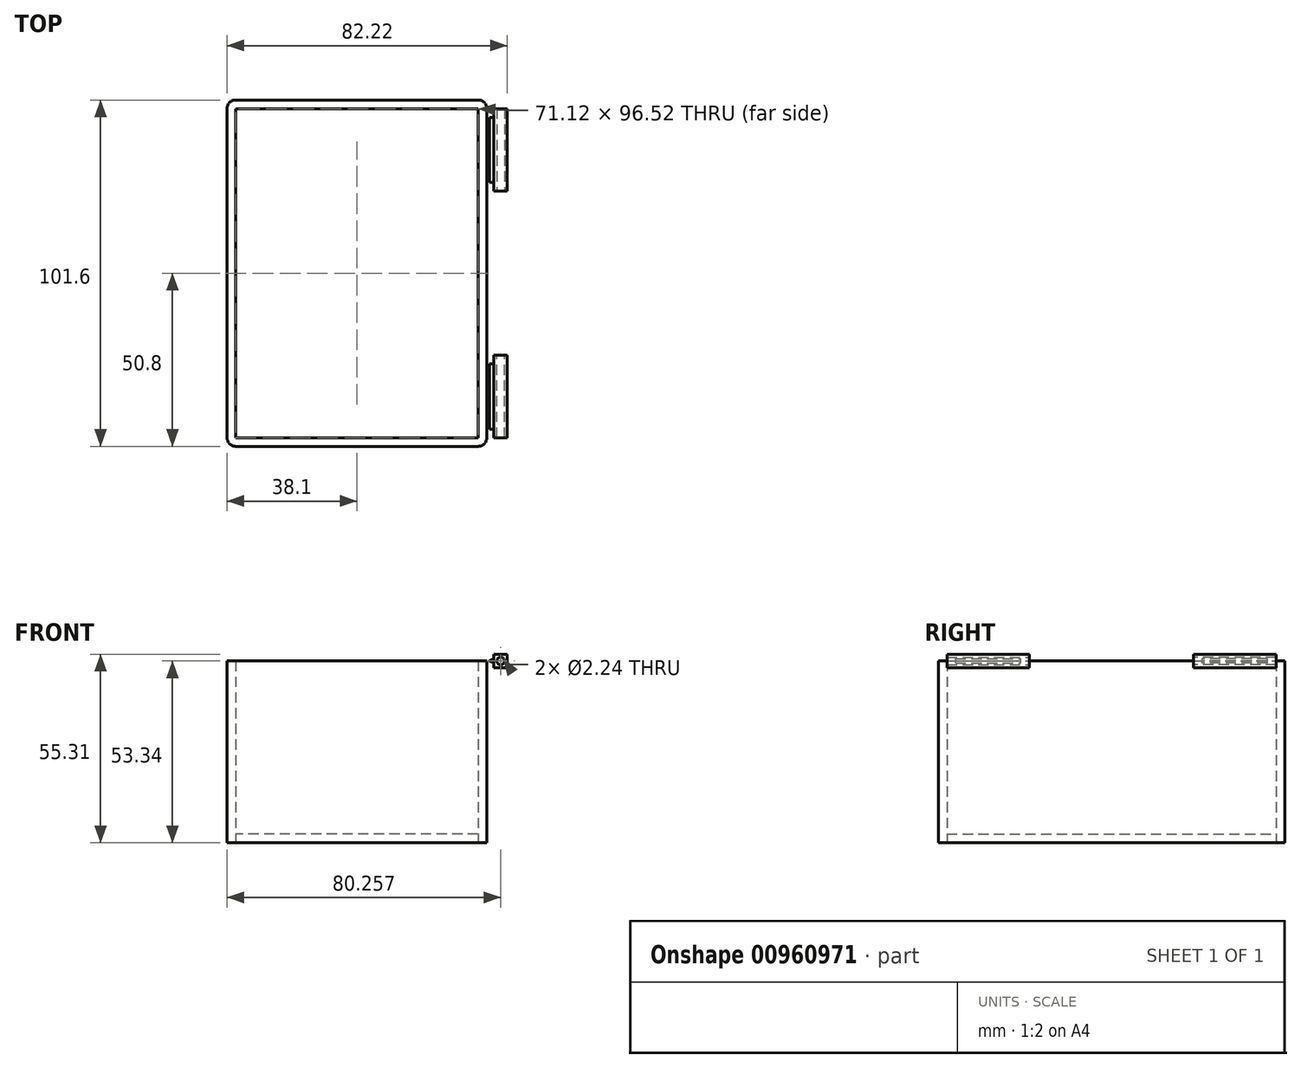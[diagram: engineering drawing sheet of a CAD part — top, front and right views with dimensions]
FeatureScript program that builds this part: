
annotation { "Feature Type Name" : "Feature", "Feature Type Description" : "" }
export const myFeature = defineFeature(function(context is Context, id is Id, definition is map)
    precondition{}
    {
        {
            var Q0;
            Q0=qCreatedBy(makeId("Top.planeOp"),FACE);
            var sketch = newSketch(context, id + "F0", { "sketchPlane" : qUnion([Q0])});
            skLineSegment(sketch, "E0.bottom", {"start": v(38.1, -50.8) * mm, "end": v(-38.1, -50.8) * mm});
            skLineSegment(sketch, "E0.top", {"start": v(38.1, 50.8) * mm, "end": v(-38.1, 50.8) * mm});
            skLineSegment(sketch, "E0.left", {"start": v(38.1, -50.8) * mm, "end": v(38.1, 50.8) * mm});
            skLineSegment(sketch, "E0.right", {"start": v(-38.1, -50.8) * mm, "end": v(-38.1, 50.8) * mm});
            skPoint(sketch, "E0.middle", {"position": v(0, 0) * mm});
            skLineSegment(sketch, "E1.bottom", {"start": v(35.56, -48.26) * mm, "end": v(-35.56, -48.26) * mm});
            skLineSegment(sketch, "E1.top", {"start": v(35.56, 48.26) * mm, "end": v(-35.56, 48.26) * mm});
            skLineSegment(sketch, "E1.left", {"start": v(35.56, -48.26) * mm, "end": v(35.56, 48.26) * mm});
            skLineSegment(sketch, "E1.right", {"start": v(-35.56, -48.26) * mm, "end": v(-35.56, 48.26) * mm});
            skSolve(sketch);
        }
        {
            var Q0;
            Q0=makeQuery(id+"F0.imprint","IMPRINT",FACE,{"disambiguationData":[TD([[makeQuery(id+"F0.imprint","IMPRINT",EDGE,{"derivedFrom":sQuery(id+"F0.wireOp",EDGE,"E0.bottom")}),-1.0]])]});
            extrude(context, id + "F1", {"entities" : qUnion([Q0]), "depth" : 53.34 * mm, "offsetDistance" : 25.4 * mm});
        }
        {
            var Q0;
            Q0=makeQuery(id+"F0.imprint","IMPRINT",FACE,{"disambiguationData":[TD([[makeQuery(id+"F0.imprint","IMPRINT",EDGE,{"derivedFrom":sQuery(id+"F0.wireOp",EDGE,"E1.bottom")}),-1.0]])]});
            extrude(context, id + "F2", {"entities" : qUnion([Q0]), "depth" : 2.54 * mm, "offsetDistance" : 25.4 * mm});
        }
        {
            var Q0;
            Q0=makeQuery(id+"F1.opExtrude","SWEPT_EDGE",EDGE,{"disambiguationData":[OSD([sQuery(id+"F0.wireOp",EDGE,"E0.top"),sQuery(id+"F0.wireOp",EDGE,"E0.left")])]});
            var Q1;
            Q1=makeQuery(id+"F1.opExtrude","SWEPT_EDGE",EDGE,{"disambiguationData":[OSD([sQuery(id+"F0.wireOp",EDGE,"E0.bottom"),sQuery(id+"F0.wireOp",EDGE,"E0.left")])]});
            var Q2;
            Q2=makeQuery(id+"F1.opExtrude","SWEPT_EDGE",EDGE,{"disambiguationData":[OSD([sQuery(id+"F0.wireOp",EDGE,"E0.top"),sQuery(id+"F0.wireOp",EDGE,"E0.right")])]});
            var Q3;
            Q3=makeQuery(id+"F1.opExtrude","SWEPT_EDGE",EDGE,{"disambiguationData":[OSD([sQuery(id+"F0.wireOp",EDGE,"E0.bottom"),sQuery(id+"F0.wireOp",EDGE,"E0.right")])]});
            fillet(context, id + "F3", {"entities" : qUnion([Q0, Q1, Q2, Q3]), "radius" : 2.54 * mm, "tangentPropagation" : true, "allowEdgeOverflow" : false});
        }
        {
            var Q0;
            Q0=qCreatedBy(makeId("Front.planeOp"),FACE);
            var sketch = newSketch(context, id + "F4", { "sketchPlane" : qUnion([Q0])});
            skPoint(sketch, "E2", {"position": v(0, 55.07) * mm});
            skLineSegment(sketch, "E3.bottom", {"start": v(38.1, 53.34) * mm, "end": v(-38.1, 53.34) * mm});
            skLineSegment(sketch, "E3.top", {"start": v(38.1, 56.8) * mm, "end": v(-38.1, 56.8) * mm});
            skLineSegment(sketch, "E3.left", {"start": v(38.1, 53.34) * mm, "end": v(38.1, 56.8) * mm});
            skLineSegment(sketch, "E3.right", {"start": v(-38.1, 53.34) * mm, "end": v(-38.1, 56.8) * mm});
            skPoint(sketch, "E4", {"position": v(0, 52.33) * mm});
            skLineSegment(sketch, "E5.bottom", {"start": v(35.3, 51.31) * mm, "end": v(-35.3, 51.31) * mm});
            skLineSegment(sketch, "E5.top", {"start": v(35.3, 53.34) * mm, "end": v(-35.3, 53.34) * mm});
            skLineSegment(sketch, "E5.left", {"start": v(35.3, 51.31) * mm, "end": v(35.3, 53.34) * mm});
            skLineSegment(sketch, "E5.right", {"start": v(-35.3, 51.31) * mm, "end": v(-35.3, 53.34) * mm});
            skCircle(sketch, "E6", {"center": v(42.16, 53.34) * mm, "radius": 1.46 * mm});
            skPoint(sketch, "E6.centerSnap0", {"position": v(0, 53.34) * mm});
            skLineSegment(sketch, "E7", {"start": v(41.22, 52.22) * mm, "end": v(38.1, 53.8) * mm});
            skCircle(sketch, "E8", {"center": v(42.16, 53.34) * mm, "radius": 1.12 * mm});
            skLineSegment(sketch, "E9", {"start": v(42.16, 54.8) * mm, "end": v(38.1, 56.8) * mm});
            skLineSegment(sketch, "E10", {"start": v(38.16, 53.12) * mm, "end": v(41.49, 54.64) * mm});
            skLineSegment(sketch, "E11", {"start": v(42.6, 51.95) * mm, "end": v(38.02, 50.36) * mm});
            skLineSegment(sketch, "E12", {"start": v(38.1, 53.34) * mm, "end": v(38.02, 50.36) * mm});
            skLineSegment(sketch, "E13", {"start": v(38.83, 53.43) * mm, "end": v(38.16, 53.12) * mm});
            skLineSegment(sketch, "E14", {"start": v(38.16, 53.12) * mm, "end": v(38.1, 53.09) * mm});
            skLineSegment(sketch, "E15.bottom", {"start": v(44.12, 51.37) * mm, "end": v(40.2, 51.37) * mm});
            skLineSegment(sketch, "E15.top", {"start": v(44.12, 55.31) * mm, "end": v(40.2, 55.31) * mm});
            skLineSegment(sketch, "E15.left", {"start": v(44.12, 51.37) * mm, "end": v(44.12, 55.31) * mm});
            skLineSegment(sketch, "E15.right", {"start": v(40.2, 51.37) * mm, "end": v(40.2, 55.31) * mm});
            skSolve(sketch);
        }
        {
            var Q0;
            Q0=makeQuery(id+"F4.imprint","IMPRINT",FACE,{"disambiguationData":[TD([[makeQuery(id+"F4.imprint","IMPRINT",EDGE,{"derivedFrom":sQuery(id+"F4.wireOp",EDGE,"E8")}),-1.0]])]});
            var Q1;
            {var subQ5=sQuery(id+"F4.wireOp",EDGE,"E15.left");Q1=makeQuery(id+"F4.imprint","IMPRINT",FACE,{"disambiguationData":[TD([[makeQuery(id+"F4.imprint","IMPRINT",EDGE,{"derivedFrom":subQ5}),1.0]])]});}
            var Q2;
            {var subQ0=sQuery(id+"F4.wireOp",EDGE,"E7");var subQ1=sQuery(id+"F4.wireOp",EDGE,"E6");var subQ2=makeQuery(id+"F4.imprint","INTERSECT",VERTEX,{"derivedFrom":[subQ1,subQ0]});Q2=makeQuery(id+"F4.imprint","IMPRINT",FACE,{"disambiguationData":[TD([[makeQuery(id+"F4.imprint","IMPRINT",EDGE,{"disambiguationData":[TD([[subQ2,1.0]])],"derivedFrom":subQ1}),-1.0]])]});}
            var Q3;
            {var subQ5=sQuery(id+"F4.wireOp",EDGE,"E7");var subQ6=sQuery(id+"F4.wireOp",EDGE,"E6");var subQ7=makeQuery(id+"F4.imprint","INTERSECT",VERTEX,{"derivedFrom":[subQ6,subQ5]});Q3=makeQuery(id+"F4.imprint","IMPRINT",FACE,{"disambiguationData":[TD([[makeQuery(id+"F4.imprint","IMPRINT",EDGE,{"disambiguationData":[TD([[subQ7,-1.0]])],"derivedFrom":subQ6}),-1.0]])]});}
            var Q4;
            {var subQ3=sQuery(id+"F4.wireOp",EDGE,"E9");var subQ6=sQuery(id+"F4.wireOp",EDGE,"E6");var subQ9=makeQuery(id+"F4.imprint","INTERSECT",VERTEX,{"derivedFrom":[subQ6,subQ3]});Q4=makeQuery(id+"F4.imprint","IMPRINT",FACE,{"disambiguationData":[TD([[makeQuery(id+"F4.imprint","IMPRINT",EDGE,{"disambiguationData":[TD([[subQ9,-1.0]])],"derivedFrom":subQ6}),-1.0]])]});}
            extrude(context, id + "F5", {"entities" : qUnion([Q0, Q1, Q2, Q3, Q4]), "depth" : 48.26 * mm, "offsetDistance" : 25.4 * mm, "hasSecondDirection" : true, "secondDirectionOppositeDirection" : false, "secondDirectionDepth" : 24.08 * mm});
        }
        {
            var Q0;
            Q0=makeQuery(id+"F4.imprint","IMPRINT",FACE,{"disambiguationData":[TD([[makeQuery(id+"F4.imprint","IMPRINT",EDGE,{"derivedFrom":sQuery(id+"F4.wireOp",EDGE,"E8")}),-1.0]])]});
            var Q1;
            {var subQ5=sQuery(id+"F4.wireOp",EDGE,"E15.left");Q1=makeQuery(id+"F4.imprint","IMPRINT",FACE,{"disambiguationData":[TD([[makeQuery(id+"F4.imprint","IMPRINT",EDGE,{"derivedFrom":subQ5}),1.0]])]});}
            var Q2;
            {var subQ3=sQuery(id+"F4.wireOp",EDGE,"E9");var subQ6=sQuery(id+"F4.wireOp",EDGE,"E6");var subQ9=makeQuery(id+"F4.imprint","INTERSECT",VERTEX,{"derivedFrom":[subQ6,subQ3]});Q2=makeQuery(id+"F4.imprint","IMPRINT",FACE,{"disambiguationData":[TD([[makeQuery(id+"F4.imprint","IMPRINT",EDGE,{"disambiguationData":[TD([[subQ9,-1.0]])],"derivedFrom":subQ6}),-1.0]])]});}
            var Q3;
            {var subQ0=sQuery(id+"F4.wireOp",EDGE,"E7");var subQ1=sQuery(id+"F4.wireOp",EDGE,"E6");var subQ2=makeQuery(id+"F4.imprint","INTERSECT",VERTEX,{"derivedFrom":[subQ1,subQ0]});Q3=makeQuery(id+"F4.imprint","IMPRINT",FACE,{"disambiguationData":[TD([[makeQuery(id+"F4.imprint","IMPRINT",EDGE,{"disambiguationData":[TD([[subQ2,1.0]])],"derivedFrom":subQ1}),-1.0]])]});}
            var Q4;
            {var subQ5=sQuery(id+"F4.wireOp",EDGE,"E7");var subQ6=sQuery(id+"F4.wireOp",EDGE,"E6");var subQ7=makeQuery(id+"F4.imprint","INTERSECT",VERTEX,{"derivedFrom":[subQ6,subQ5]});Q4=makeQuery(id+"F4.imprint","IMPRINT",FACE,{"disambiguationData":[TD([[makeQuery(id+"F4.imprint","IMPRINT",EDGE,{"disambiguationData":[TD([[subQ7,-1.0]])],"derivedFrom":subQ6}),-1.0]])]});}
            extrude(context, id + "F6", {"entities" : qUnion([Q0, Q1, Q2, Q3, Q4]), "oppositeDirection" : true, "depth" : 48.26 * mm, "offsetDistance" : 25.4 * mm, "hasSecondDirection" : true, "secondDirectionOppositeDirection" : true, "secondDirectionDepth" : 24.08 * mm});
        }
        {
            var Q0;
            {var subQ0=sQuery(id+"F4.wireOp",EDGE,"E7");var subQ1=sQuery(id+"F4.wireOp",EDGE,"E6");var subQ2=makeQuery(id+"F4.imprint","INTERSECT",VERTEX,{"derivedFrom":[subQ1,subQ0]});Q0=makeQuery(id+"F4.imprint","IMPRINT",FACE,{"disambiguationData":[TD([[makeQuery(id+"F4.imprint","IMPRINT",EDGE,{"disambiguationData":[TD([[subQ2,1.0]])],"derivedFrom":subQ1}),-1.0]])]});}
            var Q1;
            {var subQ1=sQuery(id+"F4.wireOp",EDGE,"E11");Q1=makeQuery(id+"F4.imprint","IMPRINT",FACE,{"disambiguationData":[TD([[makeQuery(id+"F4.imprint","IMPRINT",EDGE,{"derivedFrom":subQ1}),-1.0]])]});}
            var Q2;
            {var subQ0=sQuery(id+"F4.wireOp",EDGE,"E13");Q2=makeQuery(id+"F4.imprint","IMPRINT",FACE,{"disambiguationData":[TD([[makeQuery(id+"F4.imprint","IMPRINT",EDGE,{"derivedFrom":subQ0}),1.0]])]});}
            var Q3;
            {var subQ1=sQuery(id+"F4.wireOp",EDGE,"E7");var subQ3=sQuery(id+"F4.wireOp",EDGE,"E15.right");var subQ4=makeQuery(id+"F4.imprint","INTERSECT",VERTEX,{"derivedFrom":[subQ1,subQ3]});Q3=makeQuery(id+"F4.imprint","IMPRINT",FACE,{"disambiguationData":[TD([[makeQuery(id+"F4.imprint","IMPRINT",EDGE,{"disambiguationData":[TD([[subQ4,-1.0]])],"derivedFrom":subQ3}),1.0]])]});}
            extrude(context, id + "F7", {"entities" : qUnion([Q0, Q1, Q2, Q3]), "operationType" : NewBodyOperationType.ADD, "depth" : 45.72 * mm, "offsetDistance" : 25.4 * mm, "hasSecondDirection" : true, "secondDirectionOppositeDirection" : false, "secondDirectionDepth" : 26.62 * mm});
        }
        {
            var Q0;
            {var subQ1=sQuery(id+"F4.wireOp",EDGE,"E11");Q0=makeQuery(id+"F4.imprint","IMPRINT",FACE,{"disambiguationData":[TD([[makeQuery(id+"F4.imprint","IMPRINT",EDGE,{"derivedFrom":subQ1}),-1.0]])]});}
            var Q1;
            {var subQ3=sQuery(id+"F4.wireOp",EDGE,"E10");Q1=makeQuery(id+"F4.imprint","IMPRINT",FACE,{"disambiguationData":[TD([[makeQuery(id+"F4.imprint","IMPRINT",EDGE,{"derivedFrom":subQ3}),-1.0]])]});}
            var Q2;
            {var subQ0=sQuery(id+"F4.wireOp",EDGE,"E13");Q2=makeQuery(id+"F4.imprint","IMPRINT",FACE,{"disambiguationData":[TD([[makeQuery(id+"F4.imprint","IMPRINT",EDGE,{"derivedFrom":subQ0}),1.0]])]});}
            extrude(context, id + "F8", {"entities" : qUnion([Q0, Q1, Q2]), "operationType" : NewBodyOperationType.ADD, "oppositeDirection" : true, "depth" : 45.72 * mm, "offsetDistance" : 25.4 * mm, "hasSecondDirection" : true, "secondDirectionOppositeDirection" : true, "secondDirectionDepth" : 26.62 * mm});
        }
    });
